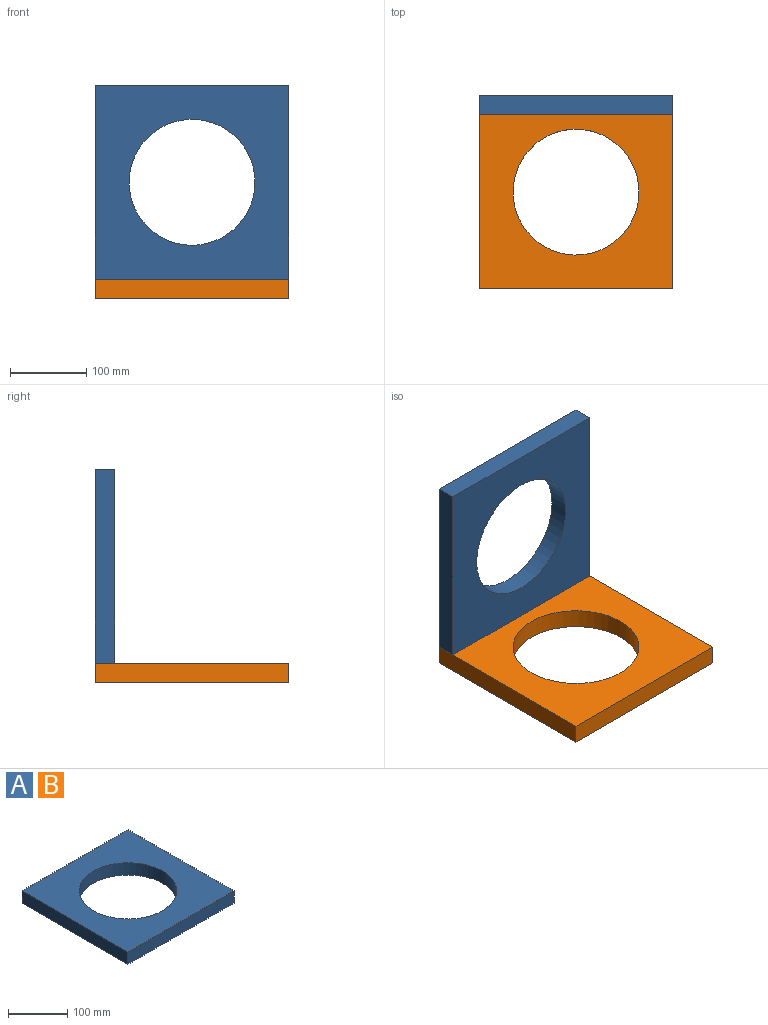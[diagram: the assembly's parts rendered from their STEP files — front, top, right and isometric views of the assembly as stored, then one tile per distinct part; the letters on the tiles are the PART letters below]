
ASSEMBLY  parts=2 mates=1
PART A: 7 faces, bbox 254x254x25.4 mm
  f0: plane 254x25.4mm, normal (-1,0,0), area 6451.6mm2, adj f1,f3,f4,f5
  f1: plane 254x25.4mm, normal (0,-1,0), area 6451.6mm2, adj f0,f2,f4,f5
  f2: plane 254x25.4mm, normal (1,0,0), area 6451.6mm2, adj f1,f3,f4,f5
  f3: plane 254x25.4mm, normal (0,1,0), area 6451.6mm2, adj f0,f2,f4,f5
  f4: plane 254x254mm, normal (0,0,1), area 43107.6mm2, adj f0,f1,f2,f3,f6
  f5: plane 254x254mm, normal (0,0,-1), area 43107.6mm2, adj f0,f1,f2,f3,f6
  f6: cylinder r=82.55mm len=165.1mm, axis (0,0,1), area 13174.4mm2, adj f4,f5
PART B: same geometry as A
PLACE A rot(axis=(1,0,0),90deg) t=(-29.71,200.27,38.35)mm
PLACE B t=(-29.71,-53.73,12.95)mm
MATE fastened A.f1 <-> B.f4  axis (0,0,-1) through (97.29,200.27,38.35)mm
